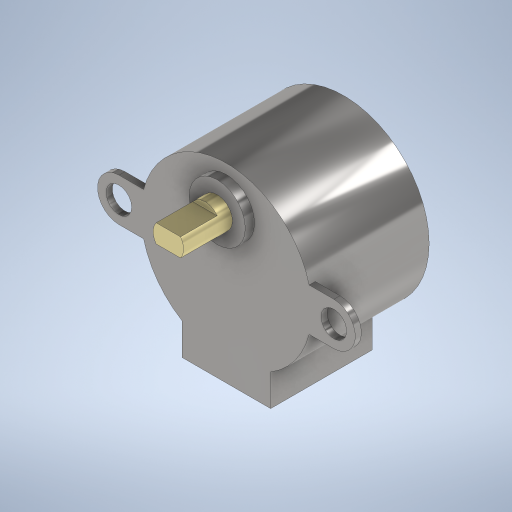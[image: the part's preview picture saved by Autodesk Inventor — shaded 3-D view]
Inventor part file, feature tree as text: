
AUTODESK INVENTOR PART (.ipt)
format: ipt  version: 2023.1 (Build 271208000, 208)  size: 329,216 bytes
history: native  units: mm
features: extrude x6, sketch x5, other x2, projected_geometry x2, mirror x1
ambient origin geometry x8: Origin, YZ Plane, XZ Plane, XY Plane, X Axis, Y Axis, Z Axis, Center Point
bodies: Body1 (feature_tree)
feature tree (16):
  other  "솔리드1"
  sketch  "스케치1"
  extrude  "돌출1"  Depth=28.0mm
  extrude  "돌출2"  Depth=5.2mm
  extrude  "돌출3"  Depth=14.5mm
  mirror  "미러1"
  extrude  "돌출4"  Depth=19.2mm TaperAngle=0.0deg
  extrude  "돌출5"  Depth=16.6mm TaperAngle=0.0deg
  extrude  "돌출6"  Depth=4.2mm
  sketch  "스케치2"
  other  "작업 평면1"
  sketch  "스케치3"
  sketch  "스케치4"
  projected_geometry  "투영된 루프1"
  sketch  "스케치5"
  projected_geometry  "투영된 루프2"
